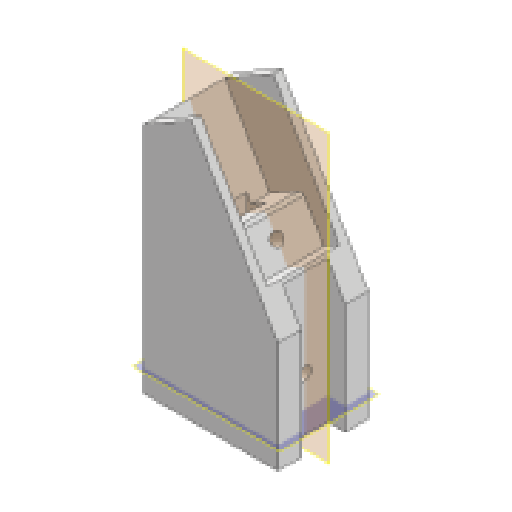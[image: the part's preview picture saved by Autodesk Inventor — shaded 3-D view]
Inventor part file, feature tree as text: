
AUTODESK INVENTOR PART (.ipt)
format: ipt  version: 2025 (Build 290162010, 162A)  size: 216,576 bytes
history: native  units: in
note: dims shown in document units (in); Inventor stores cm internally (conversion verified against a paired STEP export)
features: extrude x13, sketch x13, reference x9, other x8, plane x3, mirror x1, chamfer x1, projected_geometry x1
ambient origin geometry x8: Origin, YZ Plane, XZ Plane, XY Plane, X Axis, Y Axis, Z Axis, Center Point
bodies: Solid1 (feature_tree)
feature tree (49):
  extrude  "Extrusion1"  Depth=1.0in
  extrude  "Extrusion2"  Depth=2.6in
  plane  "Work Plane1"
  mirror  "Mirror1"
  extrude  "Extrusion3"  Depth=0.81in TaperAngle=0.0deg
  extrude  "Extrusion4"  Depth=0.5in
  extrude  "Extrusion5"  Depth=0.25in
  chamfer  "Chamfer1"  Distance=4.375in
  extrude  "Extrusion6"  Depth=0.487in
  plane  "Work Plane2"
  extrude  "Extrusion7"  Depth=0.2in TaperAngle=45.0deg
  plane  "Work Plane3"
  extrude  "Extrusion8"  Depth=0.3in TaperAngle=0.0deg
  extrude  "Extrusion9"  Depth=0.4in TaperAngle=0.0deg
  extrude  "Extrusion11"  Depth=0.5in TaperAngle=0.0deg
  extrude  "Extrusion13"  Depth=0.3012in TaperAngle=0.0deg
  extrude  "Extrusion14"  Depth=0.6in TaperAngle=0.0deg
  extrude  "Extrusion15"  Depth=0.3in
  sketch  "Sketch1"  dims[d0=0.618in d1=1.0in]
  sketch  "Sketch2"  dims[d2=1.5in d3=2.6in]
  projected_geometry  "Projected Loop1"
  sketch  "Sketch3"  dims[d4=120.0deg d5=0.81in d6=0.0in]
  sketch  "Sketch4"  dims[d7=0.1in d8=0.0in d9=0.5in]
  reference  "Reference1"
  sketch  "Sketch5"  dims[d10=0.2in d11=0.25in d12=4.375in d13=0.0in]
  sketch  "Sketch6"  dims[d14=0.6in d15=0.0in d16=0.487in]
  reference  "Reference2"
  sketch  "Sketch7"  dims[d17=0.2in d18=0.0in d19=0.04in d20=0.125in d21=45.0deg]
  reference  "Reference3"
  reference  "Reference4"
  sketch  "Sketch8"  dims[d22=0.14in d23=0.3in d24=0.0in]
  reference  "Reference5"
  reference  "Reference6"
  sketch  "Sketch9"  dims[d25=0.2in d26=0.4in d27=0.0in]
  sketch  "Sketch11"  dims[d28=-0.25in d31=0.5in d32=0.0in]
  reference  "Reference8"
  sketch  "Sketch13"  dims[d37=0.702in d38=0.3012in d39=0.0in]
  reference  "Reference12"
  sketch  "Sketch14"  dims[d42=0.6in d43=0.0in d46=0.6in d47=0.0in]
  reference  "Reference13"
  sketch  "Sketch15"  dims[d48=0.6in d49=0.0in d50=0.3in d51=0.5in d52=0.0in]
  parser-record x2  (decoder bookkeeping rows leaked as tree rows — omitted from the tree; the rows remain in map.json)
  other  "Finger Assem.iam"
  other  "KNUCKLE 4:1"
  other  "Servo Base:4"
  other  "Hand Assem.iam"
  other  "Thumb Base2:1"
  other  "Wrist Base:1"
note: 2 file-system paths scrubbed to <path> (originals preserved in map.json)
